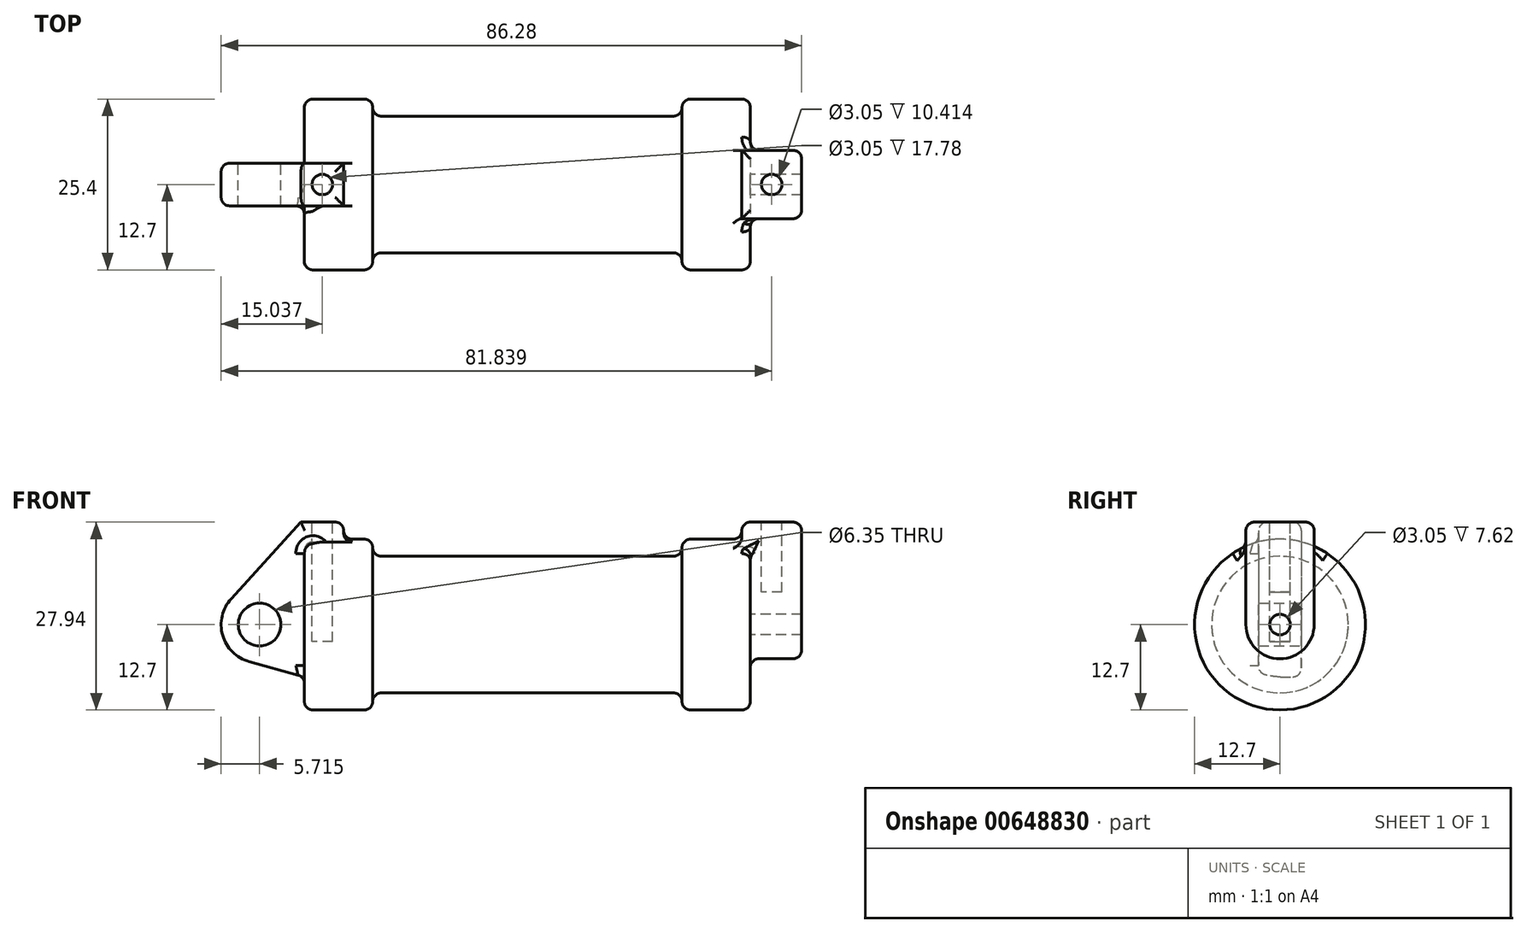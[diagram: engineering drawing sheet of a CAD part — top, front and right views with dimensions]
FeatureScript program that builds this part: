
annotation { "Feature Type Name" : "Feature", "Feature Type Description" : "" }
export const myFeature = defineFeature(function(context is Context, id is Id, definition is map)
    precondition{}
    {
        {
            var Q0;
            Q0=qCreatedBy(makeId("Front.planeOp"),FACE);
            var sketch = newSketch(context, id + "F0", { "sketchPlane" : qUnion([Q0])});
            skLineSegment(sketch, "E0", {"start": v(0, 0) * mm, "end": v(0, 12.7) * mm});
            skLineSegment(sketch, "E1", {"start": v(0, 12.7) * mm, "end": v(10.16, 12.7) * mm});
            skLineSegment(sketch, "E2", {"start": v(10.16, 12.7) * mm, "end": v(10.16, 10.16) * mm});
            skLineSegment(sketch, "E3", {"start": v(10.16, 10.16) * mm, "end": v(56.13, 10.16) * mm});
            skLineSegment(sketch, "E4", {"start": v(56.13, 10.16) * mm, "end": v(56.13, 12.7) * mm});
            skLineSegment(sketch, "E5", {"start": v(56.13, 12.7) * mm, "end": v(66.3, 12.7) * mm});
            skLineSegment(sketch, "E6", {"start": v(66.3, 12.7) * mm, "end": v(66.3, 0) * mm});
            skLineSegment(sketch, "E7", {"start": v(66.3, 0) * mm, "end": v(0, 0) * mm});
            skLineSegment(sketch, "E8", {"start": v(5.84, 15.24) * mm, "end": v(-0.5, 15.24) * mm});
            skLineSegment(sketch, "E9", {"start": v(-0.5, 15.24) * mm, "end": v(-10.88, 3.85) * mm});
            skLineSegment(sketch, "E10", {"start": v(0, 0) * mm, "end": v(-6.65, 0) * mm});
            skCircle(sketch, "E11", {"center": v(-6.65, 0) * mm, "radius": 5.72 * mm});
            skCircle(sketch, "E12", {"center": v(-6.65, 0) * mm, "radius": 3.18 * mm});
            skLineSegment(sketch, "E13", {"start": v(5.84, 15.24) * mm, "end": v(5.84, -9.4) * mm});
            skLineSegment(sketch, "E14", {"start": v(5.84, -9.4) * mm, "end": v(-8.18, -5.5) * mm});
            skSolve(sketch);
        }
        {
            var Q0;
            {var subQ0=sQuery(id+"F0.wireOp",EDGE,"E2");Q0=makeQuery(id+"F0.imprint","IMPRINT",FACE,{"disambiguationData":[TD([[makeQuery(id+"F0.imprint","IMPRINT",EDGE,{"derivedFrom":subQ0}),-1.0]])]});}
            var Q1;
            {var subQ0=sQuery(id+"F0.wireOp",EDGE,"E0");Q1=makeQuery(id+"F0.imprint","IMPRINT",FACE,{"disambiguationData":[TD([[makeQuery(id+"F0.imprint","IMPRINT",EDGE,{"derivedFrom":subQ0}),-1.0]])]});}
            var Q2;
            Q2=sQuery(id+"F0.wireOp",EDGE,"E7");
            revolve(context, id + "F1", {"entities" : qUnion([Q0, Q1]), "axis" : qUnion([Q2]), "revolveType" : RevolveType.FULL});
        }
        {
            var Q0;
            {var subQ0=sQuery(id+"F0.wireOp",EDGE,"E0");Q0=makeQuery(id+"F0.imprint","IMPRINT",FACE,{"disambiguationData":[TD([[makeQuery(id+"F0.imprint","IMPRINT",EDGE,{"derivedFrom":subQ0}),-1.0]])]});}
            var Q1;
            {var subQ1=sQuery(id+"F0.wireOp",EDGE,"E0");Q1=makeQuery(id+"F0.imprint","IMPRINT",FACE,{"disambiguationData":[TD([[makeQuery(id+"F0.imprint","IMPRINT",EDGE,{"derivedFrom":subQ1}),1.0]])]});}
            var Q2;
            {var subQ0=sQuery(id+"F0.wireOp",EDGE,"E14");Q2=makeQuery(id+"F0.imprint","IMPRINT",FACE,{"disambiguationData":[TD([[makeQuery(id+"F0.imprint","IMPRINT",EDGE,{"derivedFrom":subQ0}),-1.0]])]});}
            var Q3;
            {var subQ5=sQuery(id+"F0.wireOp",EDGE,"E12");Q3=makeQuery(id+"F0.imprint","IMPRINT",FACE,{"disambiguationData":[TD([[makeQuery(id+"F0.imprint","IMPRINT",EDGE,{"derivedFrom":subQ5}),-1.0]])]});}
            extrude(context, id + "F2", {"entities" : qUnion([Q0, Q1, Q2, Q3]), "endBound" : BoundingType.SYMMETRIC, "depth" : 6.35 * mm, "offsetDistance" : 25.4 * mm});
        }
        {
            var Q0;
            Q0=makeQuery(id+"F1.opRevolve","SWEPT_BODY",BODY,{"disambiguationData":[OSD([sQuery(id+"F0.wireOp",EDGE,"E0"),sQuery(id+"F0.wireOp",EDGE,"E1"),sQuery(id+"F0.wireOp",EDGE,"E2"),sQuery(id+"F0.wireOp",EDGE,"E3"),sQuery(id+"F0.wireOp",EDGE,"E4"),sQuery(id+"F0.wireOp",EDGE,"E5"),sQuery(id+"F0.wireOp",EDGE,"E6"),sQuery(id+"F0.wireOp",EDGE,"E7")])]});
            var Q1;
            Q1=makeQuery(id+"F2.opExtrude","SWEPT_BODY",BODY,{"disambiguationData":[OSD([sQuery(id+"F0.wireOp",EDGE,"E8"),sQuery(id+"F0.wireOp",EDGE,"E9"),sQuery(id+"F0.wireOp",EDGE,"E11"),sQuery(id+"F0.wireOp",EDGE,"E12"),sQuery(id+"F0.wireOp",EDGE,"E13"),sQuery(id+"F0.wireOp",EDGE,"E14")])]});
            booleanBodies(context, id + "F3", {"operationType" : BooleanOperationType.UNION, "tools" : qUnion([Q0, Q1])});
        }
        {
            var Q0;
            Q0=makeQuery(id+"F1.opRevolve","SWEPT_FACE",FACE,{"disambiguationData":[OSD([sQuery(id+"F0.wireOp",EDGE,"E6")])]});
            var sketch = newSketch(context, id + "F4", { "sketchPlane" : qUnion([Q0])});
            skCircle(sketch, "E15", {"center": v(0, 0) * mm, "radius": 1.52 * mm});
            skCircle(sketch, "E16", {"center": v(0, 0) * mm, "radius": 5.08 * mm});
            skLineSegment(sketch, "E17", {"start": v(-5.08, 0) * mm, "end": v(-5.08, 15.24) * mm});
            skLineSegment(sketch, "E18", {"start": v(5.08, 0) * mm, "end": v(5.08, 15.24) * mm});
            skLineSegment(sketch, "E19", {"start": v(-5.08, 15.24) * mm, "end": v(5.08, 15.24) * mm});
            skSolve(sketch);
        }
        {
            var Q0;
            {var subQ0=sQuery(id+"F4.wireOp",EDGE,"E19");Q0=makeQuery(id+"F4.imprint","IMPRINT",FACE,{"disambiguationData":[TD([[makeQuery(id+"F4.imprint","IMPRINT",EDGE,{"derivedFrom":subQ0}),-1.0]])]});}
            var Q1;
            {var subQ0=sQuery(id+"F4.wireOp",EDGE,"E17");var subQ1=sQuery(id+"F4.wireOp",EDGE,"E16");var subQ2=makeQuery(id+"F4.imprint","INTERSECT",VERTEX,{"derivedFrom":[subQ1,subQ0]});Q1=makeQuery(id+"F4.imprint","IMPRINT",FACE,{"disambiguationData":[TD([[makeQuery(id+"F4.imprint","IMPRINT",EDGE,{"disambiguationData":[TD([[subQ2,1.0]])],"derivedFrom":subQ1}),-1.0]])]});}
            var Q2;
            Q2=makeQuery(id+"F4.imprint","IMPRINT",FACE,{"disambiguationData":[TD([[makeQuery(id+"F4.imprint","IMPRINT",EDGE,{"derivedFrom":sQuery(id+"F4.wireOp",EDGE,"E15")}),-1.0]])]});
            extrude(context, id + "F5", {"entities" : qUnion([Q0, Q1, Q2]), "operationType" : NewBodyOperationType.ADD, "depth" : 7.62 * mm, "offsetDistance" : 25.4 * mm, "hasSecondDirection" : true, "secondDirectionOppositeDirection" : true, "secondDirectionDepth" : 1.27 * mm});
        }
        {
            var Q0;
            Q0=makeQuery(id+"F5.opExtrude","SWEPT_FACE",FACE,{"disambiguationData":[OSD([sQuery(id+"F4.wireOp",EDGE,"E19")])]});
            var sketch = newSketch(context, id + "F6", { "sketchPlane" : qUnion([Q0])});
            skLineSegment(sketch, "E20", {"start": v(69.47, -7) * mm, "end": v(69.47, 7) * mm, "construction": true});
            skPoint(sketch, "E20.startSnap0", {"position": v(69.47, -5.08) * mm});
            skLineSegment(sketch, "E21", {"start": v(76.04, 0) * mm, "end": v(63.51, 0) * mm, "construction": true});
            skPoint(sketch, "E21.startSnap0", {"position": v(73.91, 0) * mm});
            skCircle(sketch, "E22", {"center": v(69.47, 0) * mm, "radius": 1.52 * mm});
            skSolve(sketch);
        }
        {
            var Q0;
            Q0=makeQuery(id+"F6.imprint","IMPRINT",FACE,{"disambiguationData":[TD([[makeQuery(id+"F6.imprint","IMPRINT",EDGE,{"derivedFrom":sQuery(id+"F6.wireOp",EDGE,"E22")}),1.0]])]});
            var Q1;
            Q1=sQuery(id+"F6.wireOp",EDGE,"E22");
            extrude(context, id + "F7", {"entities" : qUnion([Q0]), "operationType" : NewBodyOperationType.REMOVE, "surfaceEntities" : qUnion([Q1]), "oppositeDirection" : true, "depth" : 10.4 * mm, "offsetDistance" : 25.4 * mm});
        }
        {
            var Q0;
            Q0=makeQuery(id+"F2.opExtrude","SWEPT_FACE",FACE,{"disambiguationData":[OSD([sQuery(id+"F0.wireOp",EDGE,"E8")])]});
            var sketch = newSketch(context, id + "F8", { "sketchPlane" : qUnion([Q0])});
            skLineSegment(sketch, "E23", {"start": v(-1.93, 0) * mm, "end": v(7.49, 0) * mm, "construction": true});
            skPoint(sketch, "E23.startSnap0", {"position": v(-0.5, 0) * mm});
            skPoint(sketch, "E23.endSnap0", {"position": v(5.84, 0) * mm});
            skPoint(sketch, "E24.startSnap0", {"position": v(2.67, 3.18) * mm});
            skPoint(sketch, "E24.endSnap0", {"position": v(2.78, 0) * mm});
            skLineSegment(sketch, "E25", {"start": v(2.67, 4.26) * mm, "end": v(2.67, -4.14) * mm, "construction": true});
            skCircle(sketch, "E26", {"center": v(2.67, 0) * mm, "radius": 1.52 * mm});
            skSolve(sketch);
        }
        {
            var Q0;
            Q0=makeQuery(id+"F8.imprint","IMPRINT",FACE,{"disambiguationData":[TD([[makeQuery(id+"F8.imprint","IMPRINT",EDGE,{"derivedFrom":sQuery(id+"F8.wireOp",EDGE,"E26")}),1.0]])]});
            extrude(context, id + "F9", {"entities" : qUnion([Q0]), "operationType" : NewBodyOperationType.REMOVE, "oppositeDirection" : true, "depth" : 17.78 * mm, "offsetDistance" : 25.4 * mm});
        }
        {
            var Q0;
            Q0=makeQuery(id+"F1.opRevolve","SWEPT_EDGE",EDGE,{"disambiguationData":[OSD([sQuery(id+"F0.wireOp",EDGE,"E1"),sQuery(id+"F0.wireOp",EDGE,"E2")])]});
            var Q1;
            Q1=makeQuery(id+"F1.opRevolve","SWEPT_EDGE",EDGE,{"disambiguationData":[OSD([sQuery(id+"F0.wireOp",EDGE,"E0"),sQuery(id+"F0.wireOp",EDGE,"E1")])]});
            var Q2;
            Q2=makeQuery(id+"F3.opBoolean","INTERSECT",EDGE,{"derivedFrom":[makeQuery(id+"F1.opRevolve","SWEPT_FACE",FACE,{"disambiguationData":[OSD([sQuery(id+"F0.wireOp",EDGE,"E0")])]}),makeQuery(id+"F2.opExtrude","CAP_FACE",FACE,{"disambiguationData":[OSD([sQuery(id+"F0.wireOp",EDGE,"E8"),sQuery(id+"F0.wireOp",EDGE,"E9"),sQuery(id+"F0.wireOp",EDGE,"E11"),sQuery(id+"F0.wireOp",EDGE,"E12"),sQuery(id+"F0.wireOp",EDGE,"E13"),sQuery(id+"F0.wireOp",EDGE,"E14")])],"isStart":false})]});
            var Q3;
            Q3=makeQuery(id+"F2.opExtrude","CAP_EDGE",EDGE,{"disambiguationData":[OSD([sQuery(id+"F0.wireOp",EDGE,"E9")])],"isStart":false});
            var Q4;
            Q4=makeQuery(id+"F2.opExtrude","CAP_EDGE",EDGE,{"disambiguationData":[OSD([sQuery(id+"F0.wireOp",EDGE,"E8")])],"isStart":false});
            var Q5;
            Q5=makeQuery(id+"F2.opExtrude","SWEPT_EDGE",EDGE,{"disambiguationData":[OSD([sQuery(id+"F0.wireOp",EDGE,"E8"),sQuery(id+"F0.wireOp",EDGE,"E13")])]});
            var Q6;
            Q6=makeQuery(id+"F2.opExtrude","CAP_EDGE",EDGE,{"disambiguationData":[OSD([sQuery(id+"F0.wireOp",EDGE,"E8")])],"isStart":true});
            var Q7;
            Q7=makeQuery(id+"F2.opExtrude","CAP_EDGE",EDGE,{"disambiguationData":[OSD([sQuery(id+"F0.wireOp",EDGE,"E9")])],"isStart":true});
            var Q8;
            Q8=makeQuery(id+"F1.opRevolve","SWEPT_EDGE",EDGE,{"disambiguationData":[OSD([sQuery(id+"F0.wireOp",EDGE,"E2"),sQuery(id+"F0.wireOp",EDGE,"E3")])]});
            var Q9;
            Q9=makeQuery(id+"F3.opBoolean","INTERSECT",EDGE,{"derivedFrom":[makeQuery(id+"F1.opRevolve","SWEPT_FACE",FACE,{"disambiguationData":[OSD([sQuery(id+"F0.wireOp",EDGE,"E1")])]}),makeQuery(id+"F2.opExtrude","SWEPT_FACE",FACE,{"disambiguationData":[OSD([sQuery(id+"F0.wireOp",EDGE,"E13")])]})]});
            fillet(context, id + "F10", {"entities" : qUnion([Q0, Q1, Q2, Q3, Q4, Q5, Q6, Q7, Q8, Q9]), "radius" : 1.27 * mm, "tangentPropagation" : true, "allowEdgeOverflow" : false});
        }
        {
            var Q0;
            Q0=makeQuery(id+"F5.boolean.opBoolean","INTERSECT",EDGE,{"derivedFrom":[makeQuery(id+"F1.opRevolve","SWEPT_FACE",FACE,{"disambiguationData":[OSD([sQuery(id+"F0.wireOp",EDGE,"E5")])]}),makeQuery(id+"F5.opExtrude","CAP_FACE",FACE,{"disambiguationData":[OSD([sQuery(id+"F4.wireOp",EDGE,"E15"),sQuery(id+"F4.wireOp",EDGE,"E16"),sQuery(id+"F4.wireOp",EDGE,"E17"),sQuery(id+"F4.wireOp",EDGE,"E18"),sQuery(id+"F4.wireOp",EDGE,"E19")])],"isStart":true})]});
            var Q1;
            Q1=makeQuery(id+"F5.boolean.opBoolean","INTERSECT",EDGE,{"derivedFrom":[makeQuery(id+"F1.opRevolve","SWEPT_FACE",FACE,{"disambiguationData":[OSD([sQuery(id+"F0.wireOp",EDGE,"E5")])]}),makeQuery(id+"F5.opExtrude","SWEPT_FACE",FACE,{"disambiguationData":[OSD([sQuery(id+"F4.wireOp",EDGE,"E17")])]})]});
            var Q2;
            Q2=makeQuery(id+"F5.boolean.opBoolean","INTERSECT",EDGE,{"derivedFrom":[makeQuery(id+"F1.opRevolve","SWEPT_FACE",FACE,{"disambiguationData":[OSD([sQuery(id+"F0.wireOp",EDGE,"E6")])]}),makeQuery(id+"F5.opExtrude","SWEPT_FACE",FACE,{"disambiguationData":[OSD([sQuery(id+"F4.wireOp",EDGE,"E17")])]})]});
            var Q3;
            Q3=makeQuery(id+"F5.opExtrude","CAP_EDGE",EDGE,{"disambiguationData":[OSD([sQuery(id+"F4.wireOp",EDGE,"E17")])],"isStart":false});
            var Q4;
            Q4=makeQuery(id+"F5.opExtrude","CAP_EDGE",EDGE,{"disambiguationData":[OSD([sQuery(id+"F4.wireOp",EDGE,"E19")])],"isStart":false});
            var Q5;
            Q5=makeQuery(id+"F5.opExtrude","SWEPT_EDGE",EDGE,{"disambiguationData":[OSD([sQuery(id+"F4.wireOp",EDGE,"E18"),sQuery(id+"F4.wireOp",EDGE,"E19")])]});
            var Q6;
            Q6=makeQuery(id+"F5.opExtrude","CAP_EDGE",EDGE,{"disambiguationData":[OSD([sQuery(id+"F4.wireOp",EDGE,"E19")])],"isStart":true});
            var Q7;
            Q7=makeQuery(id+"F5.opExtrude","SWEPT_EDGE",EDGE,{"disambiguationData":[OSD([sQuery(id+"F4.wireOp",EDGE,"E17"),sQuery(id+"F4.wireOp",EDGE,"E19")])]});
            var Q8;
            Q8=makeQuery(id+"F1.opRevolve","SWEPT_EDGE",EDGE,{"disambiguationData":[OSD([sQuery(id+"F0.wireOp",EDGE,"E4"),sQuery(id+"F0.wireOp",EDGE,"E5")])]});
            var Q9;
            Q9=makeQuery(id+"F1.opRevolve","SWEPT_EDGE",EDGE,{"disambiguationData":[OSD([sQuery(id+"F0.wireOp",EDGE,"E3"),sQuery(id+"F0.wireOp",EDGE,"E4")])]});
            fillet(context, id + "F11", {"entities" : qUnion([Q0, Q1, Q2, Q3, Q4, Q5, Q6, Q7, Q8, Q9]), "radius" : 1.27 * mm, "tangentPropagation" : true, "allowEdgeOverflow" : false});
        }
        {
            var Q0;
            Q0=makeQuery(id+"F1.opRevolve","SWEPT_EDGE",EDGE,{"disambiguationData":[OSD([sQuery(id+"F0.wireOp",EDGE,"E5"),sQuery(id+"F0.wireOp",EDGE,"E6")])]});
            fillet(context, id + "F12", {"entities" : qUnion([Q0]), "radius" : 1.27 * mm, "tangentPropagation" : true, "allowEdgeOverflow" : false});
        }
    });
